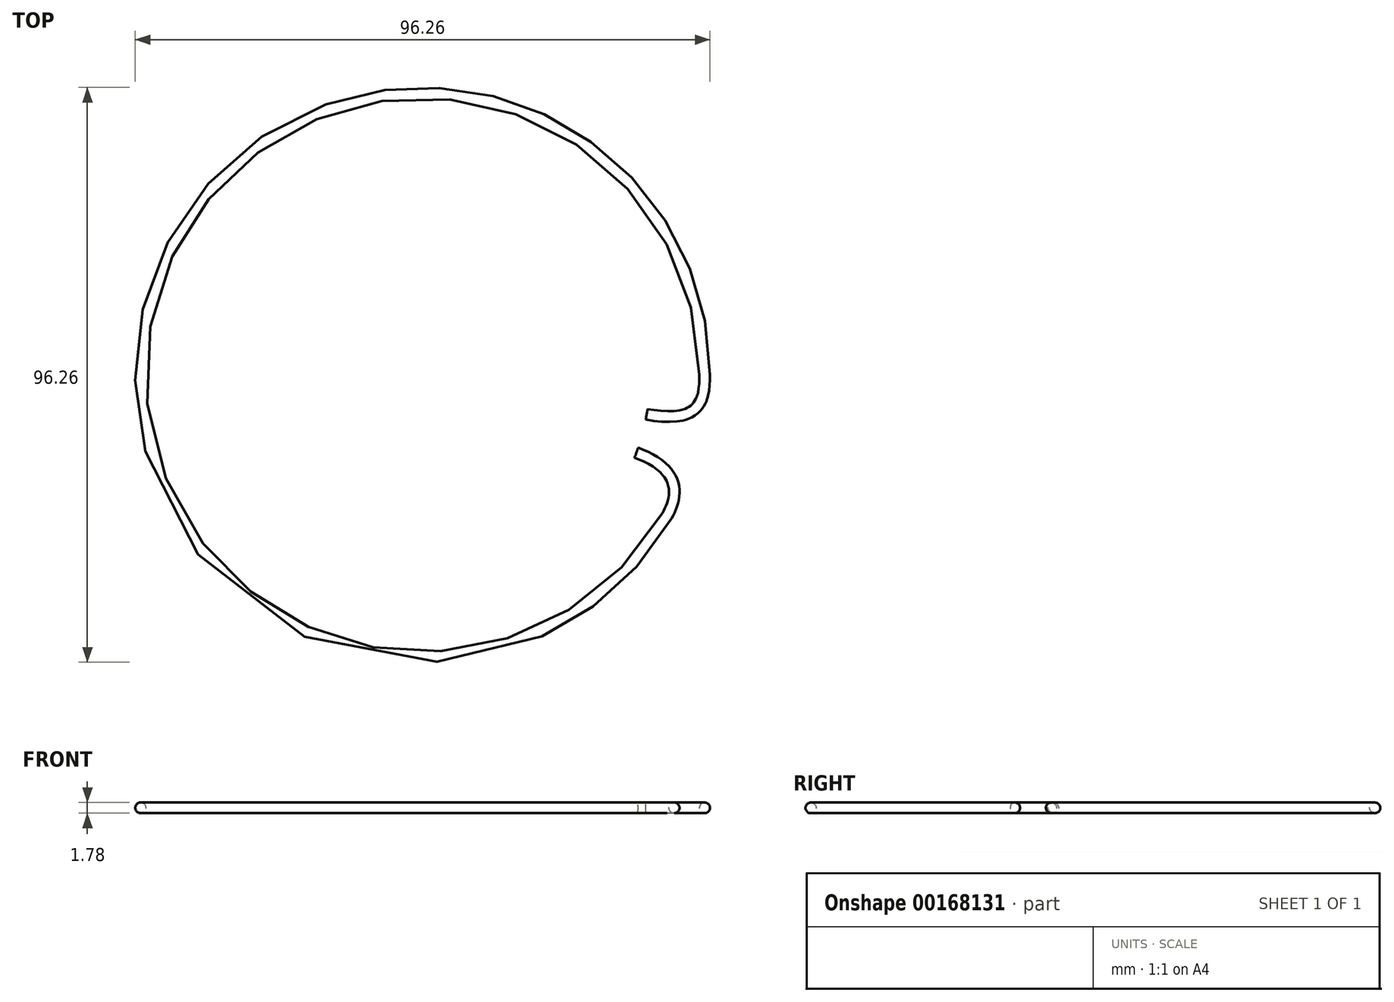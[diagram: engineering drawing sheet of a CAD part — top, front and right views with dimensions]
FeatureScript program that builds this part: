
annotation { "Feature Type Name" : "Feature", "Feature Type Description" : "" }
export const myFeature = defineFeature(function(context is Context, id is Id, definition is map)
    precondition{}
    {
        {
            var Q0;
            Q0=qCreatedBy(makeId("Front.planeOp"),FACE);
            var sketch = newSketch(context, id + "F0", { "sketchPlane" : qUnion([Q0])});
            skCircle(sketch, "E0", {"center": v(47.24, 0) * mm, "radius": 0.89 * mm});
            skSolve(sketch);
        }
        {
            var Q0;
            Q0=qCreatedBy(makeId("Top.planeOp"),FACE);
            var sketch = newSketch(context, id + "F1", { "sketchPlane" : qUnion([Q0])});
            skArc(sketch, "E1", {"start": v(47.24, 0) * mm, "mid": v(-45.63, 12.23) * mm, "end": v(40.91, -23.62) * mm});
            skFitSpline(sketch, "E2", {"points": [v(35.8, -13.03) * mm, v(40.91, -23.62) * mm], "startDerivative": vector(25.06, -9.12) * mm, "endDerivative": vector(-4.33, -7.5) * mm});
            skLineSegment(sketch, "E3", {"start": v(0, 0) * mm, "end": v(35.8, -13.03) * mm, "construction": true});
            skLineSegment(sketch, "E4", {"start": v(40.91, -23.62) * mm, "end": v(0, 0) * mm, "construction": true});
            skSolve(sketch);
        }
        {
            var Q0;
            Q0 = qSketchRegion(id + "F0", true);
            var Q1;
            Q1 = qConstructionFilter(qBodyType(qCreatedBy(id + "F0" ,EDGE), BodyType.WIRE), ConstructionObject.NO);
            var Q2;
            Q2 = qConstructionFilter(qBodyType(qCreatedBy(id + "F1" ,EDGE), BodyType.WIRE), ConstructionObject.NO);
            sweep(context, id + "F2", {"profiles" : qUnion([Q0]), "surfaceProfiles" : qUnion([Q1]), "path" : qUnion([Q2])});
        }
        {
            var Q0;
            Q0=qCreatedBy(makeId("Top.planeOp"),FACE);
            var sketch = newSketch(context, id + "F3", { "sketchPlane" : qUnion([Q0])});
            skFitSpline(sketch, "E5", {"points": [v(37.52, -6.62) * mm, v(47.24, 0) * mm], "startDerivative": vector(26.82, -4.73) * mm, "endDerivative": vector(0, 13.43) * mm});
            skLineSegment(sketch, "E6", {"start": v(0, 0) * mm, "end": v(37.52, -6.62) * mm, "construction": true});
            skSolve(sketch);
        }
        {
            var Q0;
            Q0=makeQuery(id+"F0.imprint","IMPRINT",FACE,{"disambiguationData":[TD([[makeQuery(id+"F0.imprint","IMPRINT",EDGE,{"derivedFrom":sQuery(id+"F0.wireOp",EDGE,"E0")}),1.0]])]});
            var Q1;
            Q1 = qConstructionFilter(qBodyType(qCreatedBy(id + "F3" ,EDGE), BodyType.WIRE), ConstructionObject.NO);
            sweep(context, id + "F4", {"operationType" : NewBodyOperationType.ADD, "profiles" : qUnion([Q0]), "path" : qUnion([Q1])});
        }
    });
